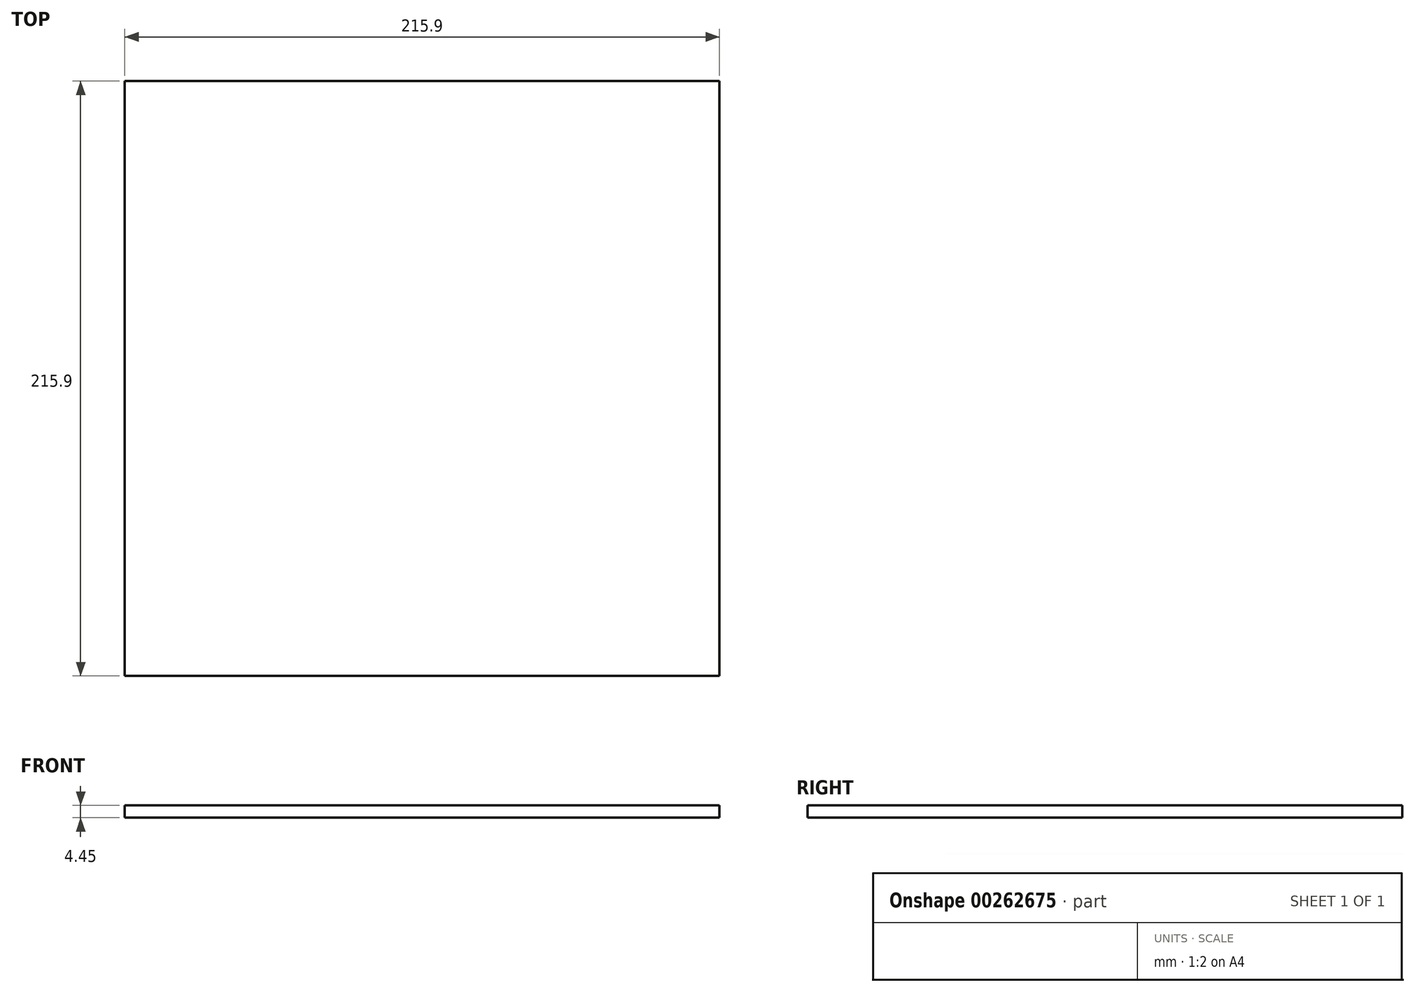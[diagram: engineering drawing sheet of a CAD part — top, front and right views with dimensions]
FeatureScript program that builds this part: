
annotation { "Feature Type Name" : "Feature", "Feature Type Description" : "" }
export const myFeature = defineFeature(function(context is Context, id is Id, definition is map)
    precondition{}
    {
        {
            var Q0;
            Q0=qCreatedBy(makeId("Top.planeOp"),FACE);
            var sketch = newSketch(context, id + "F0", { "sketchPlane" : qUnion([Q0])});
            skLineSegment(sketch, "E0.bottom", {"start": v(0, 0) * mm, "end": v(215.9, 0) * mm});
            skLineSegment(sketch, "E0.top", {"start": v(0, 215.9) * mm, "end": v(215.9, 215.9) * mm});
            skLineSegment(sketch, "E0.left", {"start": v(0, 0) * mm, "end": v(0, 215.9) * mm});
            skLineSegment(sketch, "E0.right", {"start": v(215.9, 0) * mm, "end": v(215.9, 215.9) * mm});
            skSolve(sketch);
        }
        {
            var Q0;
            Q0=makeQuery(id+"F0.imprint","IMPRINT",FACE,{"disambiguationData":[TD([[makeQuery(id+"F0.imprint","IMPRINT",EDGE,{"derivedFrom":sQuery(id+"F0.wireOp",EDGE,"E0.bottom")}),1.0]])]});
            extrude(context, id + "F1", {"entities" : qUnion([Q0]), "depth" : 4.44 * mm});
        }
    });
